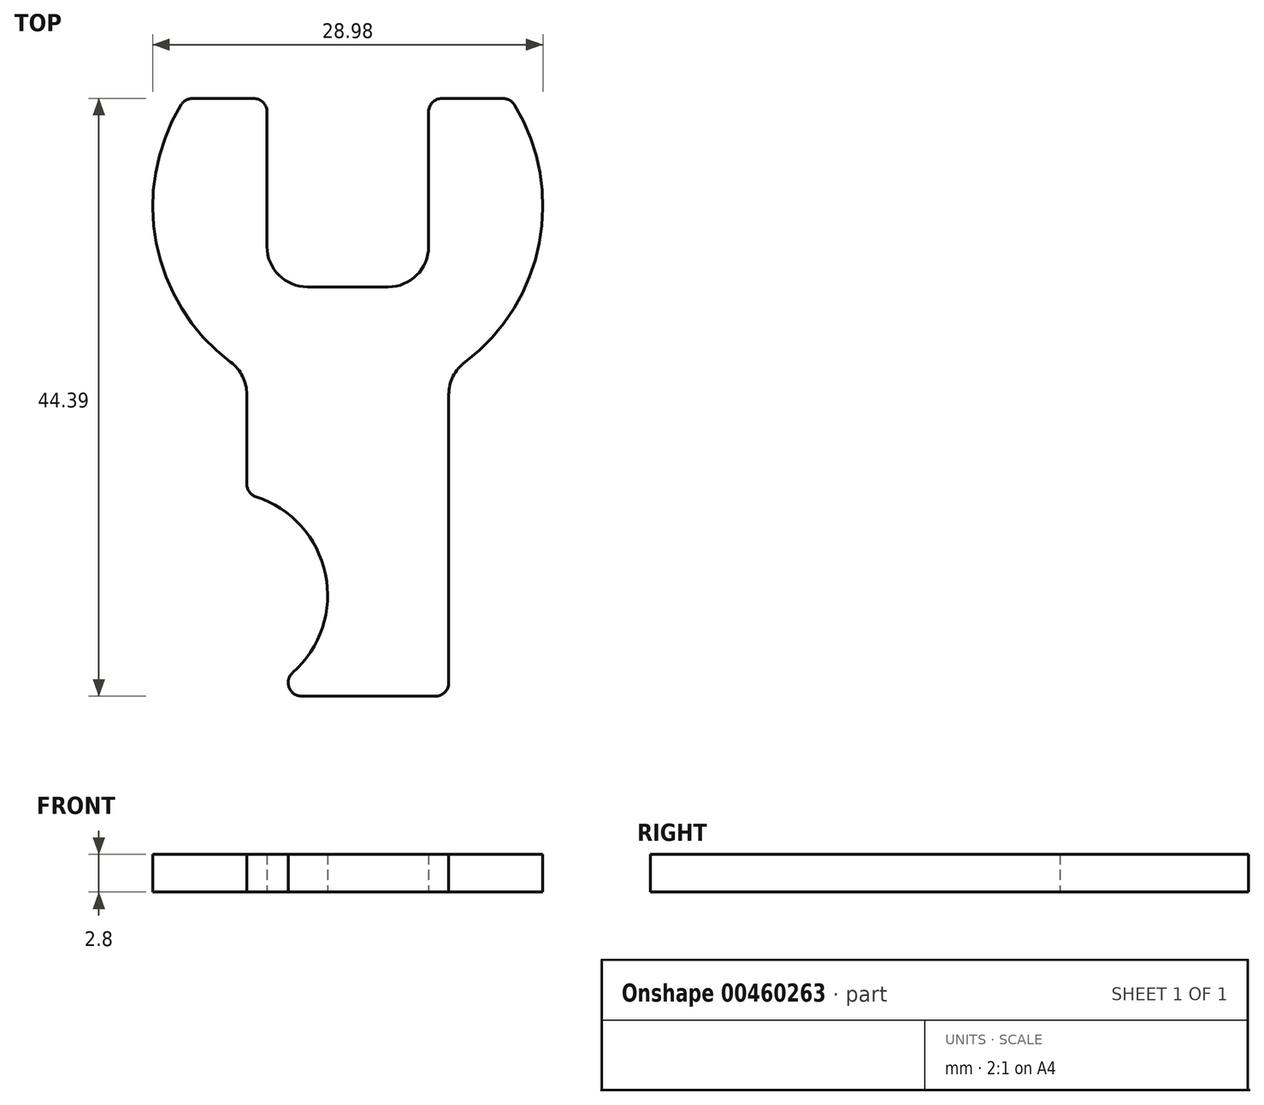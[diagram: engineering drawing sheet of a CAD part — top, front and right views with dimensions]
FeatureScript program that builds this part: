
annotation { "Feature Type Name" : "Feature", "Feature Type Description" : "" }
export const myFeature = defineFeature(function(context is Context, id is Id, definition is map)
    precondition{}
    {
        {
            var Q0;
            Q0=qCreatedBy(makeId("Top.planeOp"),FACE);
            var sketch = newSketch(context, id + "F0", { "sketchPlane" : qUnion([Q0])});
            skCircle(sketch, "E0", {"center": v(0, 0) * mm, "radius": 14.49 * mm});
            skLineSegment(sketch, "E1.bottom", {"start": v(6, 6) * mm, "end": v(-6, 6) * mm});
            skLineSegment(sketch, "E1.top", {"start": v(6, -6) * mm, "end": v(-6, -6) * mm});
            skLineSegment(sketch, "E1.left", {"start": v(6, 6) * mm, "end": v(6, -6) * mm});
            skLineSegment(sketch, "E1.right", {"start": v(-6, 6) * mm, "end": v(-6, -6) * mm});
            skLineSegment(sketch, "E2", {"start": v(6, -6) * mm, "end": v(10.24, -10.24) * mm, "construction": true});
            skLineSegment(sketch, "E3.bottom", {"start": v(-6, 6) * mm, "end": v(6, 6) * mm});
            skLineSegment(sketch, "E3.top", {"start": v(-6, 8) * mm, "end": v(6, 8) * mm});
            skLineSegment(sketch, "E3.left", {"start": v(-6, 6) * mm, "end": v(-6, 8) * mm});
            skLineSegment(sketch, "E3.right", {"start": v(6, 6) * mm, "end": v(6, 8) * mm});
            skLineSegment(sketch, "E4", {"start": v(-6, 8) * mm, "end": v(-12.08, 8) * mm});
            skLineSegment(sketch, "E5", {"start": v(6, 8) * mm, "end": v(12.08, 8) * mm});
            skLineSegment(sketch, "E6.bottom", {"start": v(7.5, -12.4) * mm, "end": v(-7.5, -12.4) * mm});
            skLineSegment(sketch, "E6.top", {"start": v(7.5, -36.4) * mm, "end": v(-7.5, -36.4) * mm});
            skLineSegment(sketch, "E6.left", {"start": v(7.5, -12.4) * mm, "end": v(7.5, -36.4) * mm});
            skLineSegment(sketch, "E6.right", {"start": v(-7.5, -12.4) * mm, "end": v(-7.5, -36.4) * mm});
            skPoint(sketch, "E6.middle", {"position": v(0, -24.4) * mm});
            skArc(sketch, "E7", {"start": v(-7.5, -36.4) * mm, "mid": v(-1.5, -28.9) * mm, "end": v(-7.5, -21.4) * mm});
            skSolve(sketch);
        }
        {
            var Q0;
            Q0=makeQuery(id+"F0.imprint","IMPRINT",FACE,{"disambiguationData":[TD([[makeQuery(id+"F0.imprint","IMPRINT",EDGE,{"derivedFrom":sQuery(id+"F0.wireOp",EDGE,"E1.top")}),1.0]])]});
            var Q1;
            Q1=makeQuery(id+"F0.imprint","IMPRINT",FACE,{"disambiguationData":[TD([[makeQuery(id+"F0.imprint","IMPRINT",EDGE,{"derivedFrom":sQuery(id+"F0.wireOp",EDGE,"E6.top")}),-1.0]])]});
            var Q2;
            {var subQ0=sQuery(id+"F0.wireOp",EDGE,"E6.bottom");Q2=makeQuery(id+"F0.imprint","IMPRINT",FACE,{"disambiguationData":[TD([[makeQuery(id+"F0.imprint","IMPRINT",EDGE,{"derivedFrom":subQ0}),1.0]])]});}
            extrude(context, id + "F1", {"entities" : qUnion([Q0, Q1, Q2]), "depth" : 2.8 * mm});
        }
        {
            var Q0;
            Q0=makeQuery(id+"F1.opExtrude","SWEPT_EDGE",EDGE,{"disambiguationData":[OSD([sQuery(id+"F0.wireOp",EDGE,"E0"),sQuery(id+"F0.wireOp",EDGE,"E6.bottom"),sQuery(id+"F0.wireOp",EDGE,"E6.right")])]});
            var Q1;
            Q1=makeQuery(id+"F1.opExtrude","SWEPT_EDGE",EDGE,{"disambiguationData":[OSD([sQuery(id+"F0.wireOp",EDGE,"E0"),sQuery(id+"F0.wireOp",EDGE,"E6.bottom"),sQuery(id+"F0.wireOp",EDGE,"E6.left")])]});
            var Q2;
            Q2=makeQuery(id+"F1.opExtrude","SWEPT_EDGE",EDGE,{"disambiguationData":[OSD([sQuery(id+"F0.wireOp",EDGE,"E1.top"),sQuery(id+"F0.wireOp",EDGE,"E1.left")])]});
            var Q3;
            Q3=makeQuery(id+"F1.opExtrude","SWEPT_EDGE",EDGE,{"disambiguationData":[OSD([sQuery(id+"F0.wireOp",EDGE,"E1.top"),sQuery(id+"F0.wireOp",EDGE,"E1.right")])]});
            fillet(context, id + "F2", {"entities" : qUnion([Q0, Q1, Q2, Q3]), "radius" : 3 * mm, "tangentPropagation" : true, "allowEdgeOverflow" : false});
        }
        {
            var Q0;
            Q0=makeQuery(id+"F1.opExtrude","SWEPT_EDGE",EDGE,{"disambiguationData":[OSD([sQuery(id+"F0.wireOp",EDGE,"E6.top"),sQuery(id+"F0.wireOp",EDGE,"E6.right"),sQuery(id+"F0.wireOp",EDGE,"E7")])]});
            var Q1;
            Q1=makeQuery(id+"F1.opExtrude","SWEPT_EDGE",EDGE,{"disambiguationData":[OSD([sQuery(id+"F0.wireOp",EDGE,"E6.right"),sQuery(id+"F0.wireOp",EDGE,"E7")])]});
            var Q2;
            Q2=makeQuery(id+"F1.opExtrude","SWEPT_EDGE",EDGE,{"disambiguationData":[OSD([sQuery(id+"F0.wireOp",EDGE,"E6.top"),sQuery(id+"F0.wireOp",EDGE,"E6.left")])]});
            var Q3;
            Q3=makeQuery(id+"F1.opExtrude","SWEPT_EDGE",EDGE,{"disambiguationData":[OSD([sQuery(id+"F0.wireOp",EDGE,"E3.top"),sQuery(id+"F0.wireOp",EDGE,"E3.right"),sQuery(id+"F0.wireOp",EDGE,"E5")])]});
            var Q4;
            Q4=makeQuery(id+"F1.opExtrude","SWEPT_EDGE",EDGE,{"disambiguationData":[OSD([sQuery(id+"F0.wireOp",EDGE,"E3.top"),sQuery(id+"F0.wireOp",EDGE,"E3.left"),sQuery(id+"F0.wireOp",EDGE,"E4")])]});
            var Q5;
            Q5=makeQuery(id+"F1.opExtrude","SWEPT_EDGE",EDGE,{"disambiguationData":[OSD([sQuery(id+"F0.wireOp",EDGE,"E0"),sQuery(id+"F0.wireOp",EDGE,"E4")])]});
            var Q6;
            Q6=makeQuery(id+"F1.opExtrude","SWEPT_EDGE",EDGE,{"disambiguationData":[OSD([sQuery(id+"F0.wireOp",EDGE,"E0"),sQuery(id+"F0.wireOp",EDGE,"E5")])]});
            fillet(context, id + "F3", {"entities" : qUnion([Q0, Q1, Q2, Q3, Q4, Q5, Q6]), "radius" : 1 * mm, "tangentPropagation" : true, "allowEdgeOverflow" : false});
        }
    });
